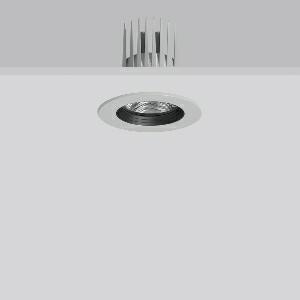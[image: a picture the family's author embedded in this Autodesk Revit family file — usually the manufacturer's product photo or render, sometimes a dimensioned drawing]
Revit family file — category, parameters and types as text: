
# Revit family: heledon_mini_e_901748_004_3_76_4754
name_source: partatom
category: Lighting Fixtures
units: mm (PartAtom-declared; Revit-internal decimal feet)

## family parameters
Cut with Voids When Loaded = No
Host = Face
Light Source = No
Part Type = Normal
Room Calculation Point = No
Round Connector Dimension = Use Diameter
Shared = No

## types (1)
- HELEDON mini E (1 x LED Modul 935, 3700 lm, 3500)
    Apparent Load = 29 VA
    Approval mark = CE
    CIE Flux Codes = 100 100 100 100 100
    Color Rendering = 92
    Color Temperature = 3500
    Default Elevation = 1800 mm
    Description = Series: HELEDON mini
Round recessed downlight. Housing: die-cast aluminium, powder-coated. Black plastic ring and recessed LED to prevent glare from the side. Optical assembly with reflector made of MIRO-Silver with 98% total light reflection for outstanding efficiency - can be changed without tools. Best colour rendering index Ra>90. Suitable for Recessed ceiling mounting. Installation without tools thanks to spring fastening system. Including separate LED converter with connecting cable 600 mm.High quality converter without flickering and stroboscopic effect. Through-wiring box (5 pole) available as accessory. The following accessories can be mounted without use of tools: interchangeable lenses, decorative glasses, honeycomb louvre, clear and frosted diffusers, white interchangeable plastic ring. 
Colour: silver
Diameter: 124 mm
Height: 3 mm
Cut-out diameter: 114 mm
Recess height: 170 mm
Luminaire: recess height: 120 mm
Lamp: LED
Socket: without socket
Colour temperature: 3500K
Colour rendering index (CRI): 92
System power: 29 W
Rated luminous flux: 3700 lm
Luminous efficiency: 128 lm/W
Control gear: Converter, dimmable, DALI
Protection class: II
Type of protection: IP 20
    Height = 0 mm  [stored 0 ft]
    Lamp = 1 x LED Modul 935
    Lamp Light Flux = 3700 lm
    Lamp count = 1
    Length = 124 mm  [stored 0.406824 ft]
    Lifetime = 50000 h
    Luminous efficacy = 128 lm/W
    Manufacturer = RZB
    ModVariant = No
    Model = 901748.004.3.76
    Mounting Place = Ceiling
    Mounting Type = Recessed
    Number of Poles = 1
    OnlyDefault = Yes
    Power Factor = 1
    Product Name = HELEDON mini E
    Product group = Recessed downlights
    ProductGroupID = 402
    Protection Class = Protection class II
    Protection Degree = IP 20
    RLX_Detail_Level = 1
    RLX_Emergency_Light_Flux = 0 lm
    RLX_Emergency_Type = 0
    RLX_Emergency_Type_DB = No
    RlxData = <blob elided: 126113 chars, md5=45f736a2>
    Socket = socket
    Standby Power = 0 W
    System Light Flux = 3700 lm
    System Power = 29 W
    Type Comments = Product without accessories
    Type Image = 901657.004.jpg
    URL = http://relux.com
    VarID = ---
    Voltage = 230 V
    Voltage Range = 220-240 V
    Weight = 0.00 kg
    Width = 0 mm  [stored 0 ft]

note: [stored X ft] marks values corroborated as IEEE doubles in the binary element streams (Revit-internal decimal feet)

## geometry (parser evidence)
native form markers: Blend x4, Sweep x11
no freeform markers — native parametric forms only
